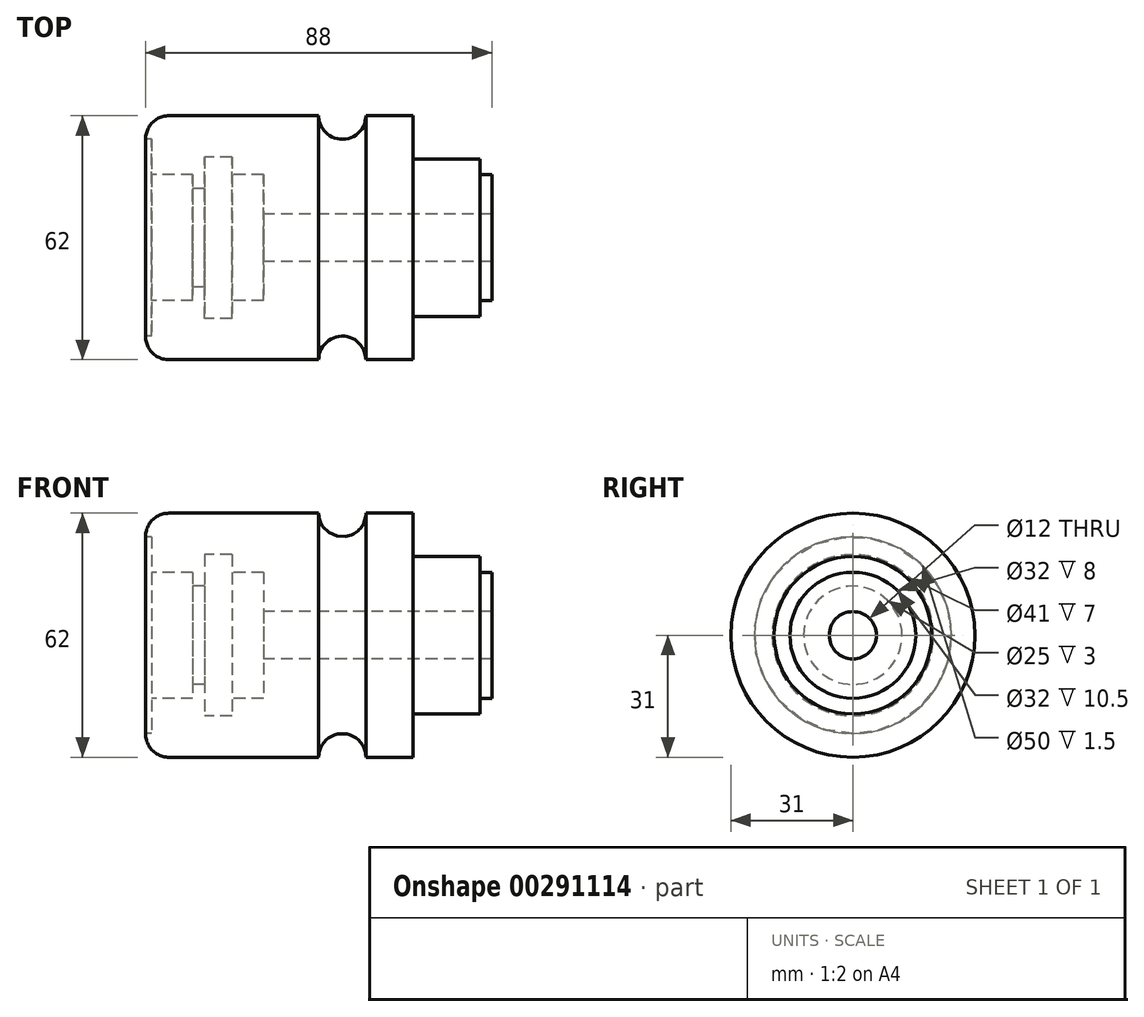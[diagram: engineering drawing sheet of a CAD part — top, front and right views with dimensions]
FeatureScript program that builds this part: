
annotation { "Feature Type Name" : "Feature", "Feature Type Description" : "" }
export const myFeature = defineFeature(function(context is Context, id is Id, definition is map)
    precondition{}
    {
        {
            var Q0;
            Q0=qCreatedBy(makeId("Front.planeOp"),FACE);
            var sketch = newSketch(context, id + "F0", { "sketchPlane" : qUnion([Q0])});
            skLineSegment(sketch, "E0", {"start": v(0, 0) * mm, "end": v(76.79, 0) * mm, "construction": true});
            skLineSegment(sketch, "E1", {"start": v(0, 0) * mm, "end": v(0, 31) * mm});
            skLineSegment(sketch, "E2", {"start": v(0, 31) * mm, "end": v(44, 31) * mm});
            skLineSegment(sketch, "E3", {"start": v(68, 31) * mm, "end": v(68, 20) * mm});
            skLineSegment(sketch, "E4", {"start": v(68, 20) * mm, "end": v(85, 20) * mm});
            skLineSegment(sketch, "E5", {"start": v(85, 20) * mm, "end": v(85, 16) * mm});
            skLineSegment(sketch, "E6", {"start": v(85, 16) * mm, "end": v(88, 16) * mm});
            skLineSegment(sketch, "E7", {"start": v(88, 16) * mm, "end": v(88, 0) * mm});
            skLineSegment(sketch, "E8", {"start": v(88, 0) * mm, "end": v(0, 0) * mm});
            skArc(sketch, "E9", {"start": v(44, 31) * mm, "mid": v(50, 25) * mm, "end": v(56, 31) * mm});
            skLineSegment(sketch, "E10.trimOffspring", {"start": v(56, 31) * mm, "end": v(68, 31) * mm});
            skSolve(sketch);
        }
        {
            var Q0;
            Q0 = qSketchRegion(id + "F0", true);
            var Q1;
            Q1=sQuery(id+"F0.wireOp",EDGE,"E8");
            revolve(context, id + "F1", {"entities" : qUnion([Q0]), "axis" : qUnion([Q1]), "revolveType" : RevolveType.FULL});
        }
        {
            var Q0;
            Q0=qCreatedBy(makeId("Front.planeOp"),FACE);
            var sketch = newSketch(context, id + "F2", { "sketchPlane" : qUnion([Q0])});
            skLineSegment(sketch, "E11", {"start": v(0, 0) * mm, "end": v(0, 25) * mm});
            skLineSegment(sketch, "E12", {"start": v(0, 25) * mm, "end": v(1.5, 25) * mm});
            skLineSegment(sketch, "E13", {"start": v(1.5, 25) * mm, "end": v(1.5, 16) * mm});
            skLineSegment(sketch, "E14", {"start": v(1.5, 16) * mm, "end": v(12, 16) * mm});
            skLineSegment(sketch, "E15", {"start": v(12, 16) * mm, "end": v(12, 12.5) * mm});
            skLineSegment(sketch, "E16", {"start": v(12, 12.5) * mm, "end": v(15, 12.5) * mm});
            skLineSegment(sketch, "E17", {"start": v(15, 12.5) * mm, "end": v(15, 20.5) * mm});
            skLineSegment(sketch, "E18", {"start": v(15, 20.5) * mm, "end": v(22, 20.5) * mm});
            skLineSegment(sketch, "E19", {"start": v(22, 20.5) * mm, "end": v(22, 16) * mm});
            skLineSegment(sketch, "E20", {"start": v(22, 16) * mm, "end": v(30, 16) * mm});
            skLineSegment(sketch, "E21", {"start": v(30, 16) * mm, "end": v(30, 6) * mm});
            skLineSegment(sketch, "E22", {"start": v(30, 6) * mm, "end": v(88, 6) * mm});
            skLineSegment(sketch, "E23", {"start": v(88, 6) * mm, "end": v(88, 0) * mm});
            skLineSegment(sketch, "E24", {"start": v(88, 0) * mm, "end": v(0, 0) * mm});
            skLineSegment(sketch, "E25", {"start": v(0, 0) * mm, "end": v(-30.62, 0) * mm, "construction": true});
            skSolve(sketch);
        }
        {
            var Q0;
            Q0 = qSketchRegion(id + "F2", true);
            var Q1;
            Q1=sQuery(id+"F2.wireOp",EDGE,"E25");
            revolve(context, id + "F3", {"operationType" : NewBodyOperationType.REMOVE, "entities" : qUnion([Q0]), "axis" : qUnion([Q1]), "revolveType" : RevolveType.FULL, "oppositeDirection" : true});
        }
        {
            var Q0;
            Q0=makeQuery(id+"F1.opRevolve","SWEPT_EDGE",EDGE,{"disambiguationData":[OSD([sQuery(id+"F0.wireOp",EDGE,"E1"),sQuery(id+"F0.wireOp",EDGE,"E2")])]});
            fillet(context, id + "F4", {"entities" : qUnion([Q0]), "radius" : 6 * mm, "tangentPropagation" : true, "allowEdgeOverflow" : false});
        }
    });
